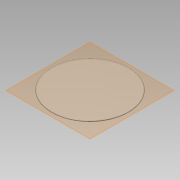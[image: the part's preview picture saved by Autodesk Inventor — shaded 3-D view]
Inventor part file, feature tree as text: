
AUTODESK INVENTOR PART (.ipt)
format: ipt  version: 2014 (Build 180170000, 170)  size: 87,552 bytes
history: native  units: mm
features: plane x1, extrude x1, fillet x1, sketch x1, reference x1
ambient origin geometry x8: Origin, YZ Plane, XZ Plane, XY Plane, X Axis, Y Axis, Z Axis, Center Point
bodies: Solid1 (feature_tree)
feature tree (5):
  plane  "Work Plane1"
  extrude  "Extrusion1"  Depth=1.0mm
  fillet  "Fillet1"  [1 undecoded]
  sketch  "Sketch1"  dims[d0=3.0mm d1=0.0mm d2=1.0mm]
  reference  "Reference1"
note: 1 required parameter value undecoded (feature->parameter linkage not recoverable at this tier; creation-order binding heuristic only, values carry confidence <= 0.55)
